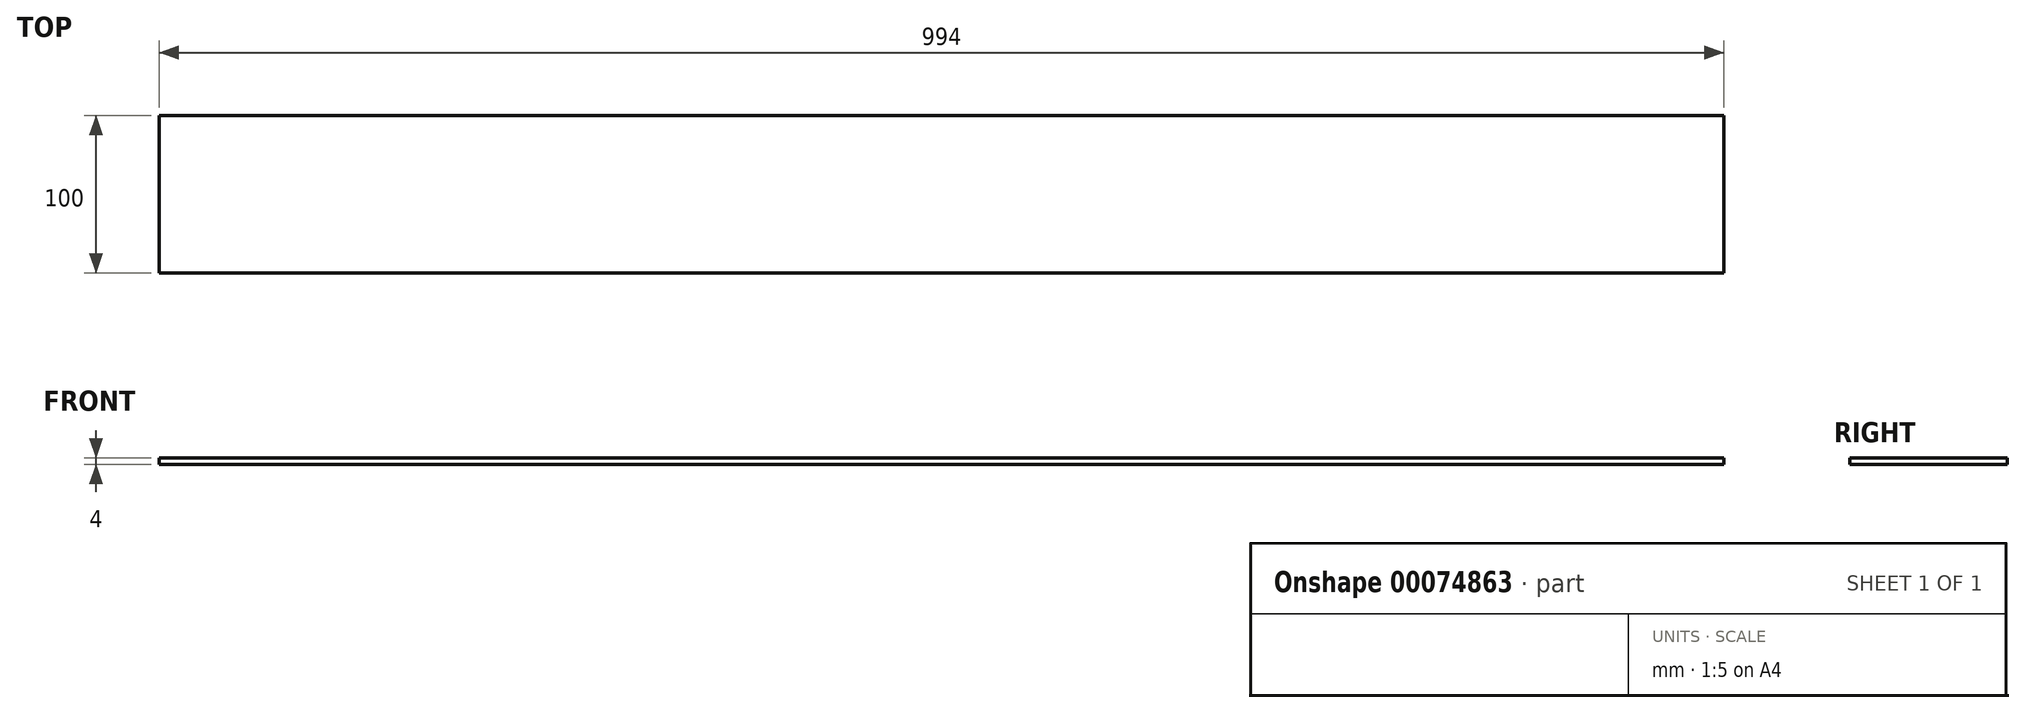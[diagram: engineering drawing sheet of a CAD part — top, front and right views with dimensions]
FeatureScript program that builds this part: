
annotation { "Feature Type Name" : "Feature", "Feature Type Description" : "" }
export const myFeature = defineFeature(function(context is Context, id is Id, definition is map)
    precondition{}
    {
        {
            var Q0;
            Q0=qCreatedBy(makeId("Top.planeOp"),FACE);
            var sketch = newSketch(context, id + "F0", { "sketchPlane" : qUnion([Q0])});
            skLineSegment(sketch, "E0.bottom", {"start": v(0, 0) * mm, "end": v(994, 0) * mm});
            skLineSegment(sketch, "E0.top", {"start": v(0, 100) * mm, "end": v(994, 100) * mm});
            skLineSegment(sketch, "E0.left", {"start": v(0, 0) * mm, "end": v(0, 100) * mm});
            skLineSegment(sketch, "E0.right", {"start": v(994, 0) * mm, "end": v(994, 100) * mm});
            skLineSegment(sketch, "E1.0", {"start": v(161, 0) * mm, "end": v(161, 100) * mm});
            skLineSegment(sketch, "E2.0", {"start": v(169.25, 0) * mm, "end": v(169.25, 100) * mm});
            skLineSegment(sketch, "E3.0", {"start": v(177.5, 0) * mm, "end": v(177.5, 100) * mm});
            skLineSegment(sketch, "E4.0", {"start": v(319.5, 0) * mm, "end": v(319.5, 100) * mm});
            skLineSegment(sketch, "E5.0", {"start": v(327.75, 0) * mm, "end": v(327.75, 100) * mm});
            skLineSegment(sketch, "E6.0", {"start": v(336, 0) * mm, "end": v(336, 100) * mm});
            skLineSegment(sketch, "E7.0", {"start": v(658, 0) * mm, "end": v(658, 100) * mm});
            skLineSegment(sketch, "E8.0", {"start": v(666.25, 0) * mm, "end": v(666.25, 100) * mm});
            skLineSegment(sketch, "E9.0", {"start": v(674.5, 0) * mm, "end": v(674.5, 100) * mm});
            skLineSegment(sketch, "E10.0", {"start": v(816.5, 0) * mm, "end": v(816.5, 100) * mm});
            skLineSegment(sketch, "E11.0", {"start": v(824.75, 0) * mm, "end": v(824.75, 100) * mm});
            skLineSegment(sketch, "E12.0", {"start": v(833, 0) * mm, "end": v(833, 100) * mm});
            skSolve(sketch);
        }
        {
            var Q0;
            Q0 = qSketchRegion(id + "F0", true);
            extrude(context, id + "F1", {"entities" : qUnion([Q0]), "oppositeDirection" : true, "depth" : 4 * mm});
        }
    });
